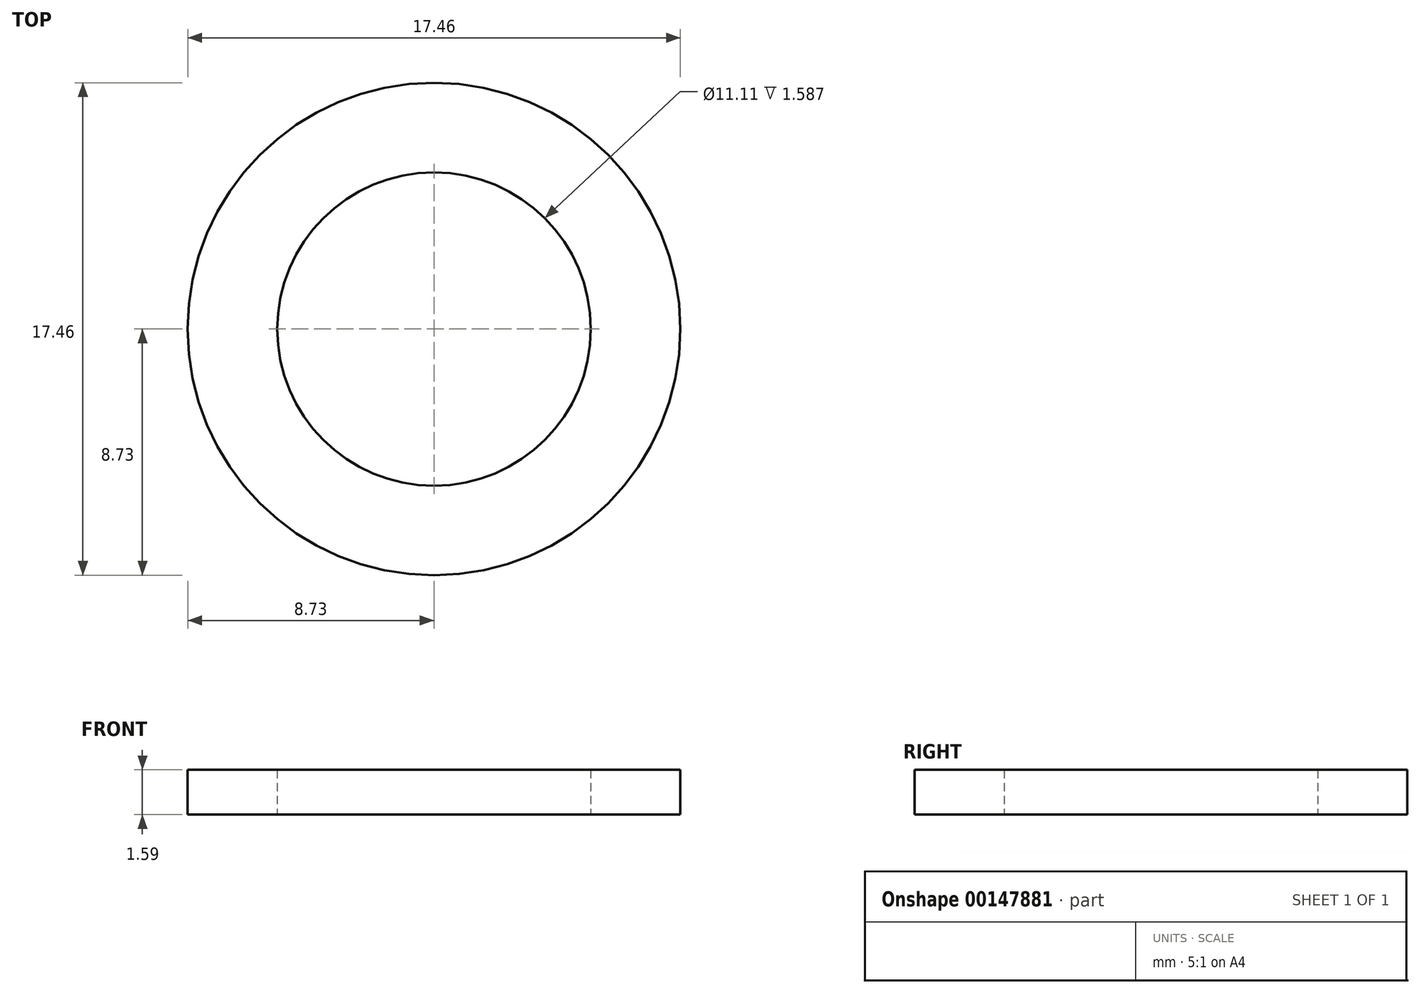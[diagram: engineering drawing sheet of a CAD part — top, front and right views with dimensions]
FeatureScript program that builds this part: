
annotation { "Feature Type Name" : "Feature", "Feature Type Description" : "" }
export const myFeature = defineFeature(function(context is Context, id is Id, definition is map)
    precondition{}
    {
        {
            var Q0;
            Q0=qCreatedBy(makeId("Top.planeOp"),FACE);
            var sketch = newSketch(context, id + "F0", { "sketchPlane" : qUnion([Q0])});
            skCircle(sketch, "E0", {"center": v(0, 0) * mm, "radius": 5.56 * mm});
            skCircle(sketch, "E1", {"center": v(0, 0) * mm, "radius": 8.73 * mm});
            skSolve(sketch);
        }
        {
            var Q0;
            Q0=qSketchRegion(id+"F0",true);
            extrude(context, id + "F1", {"entities" : qUnion([Q0]), "depth" : 1.59 * mm});
        }
    });
